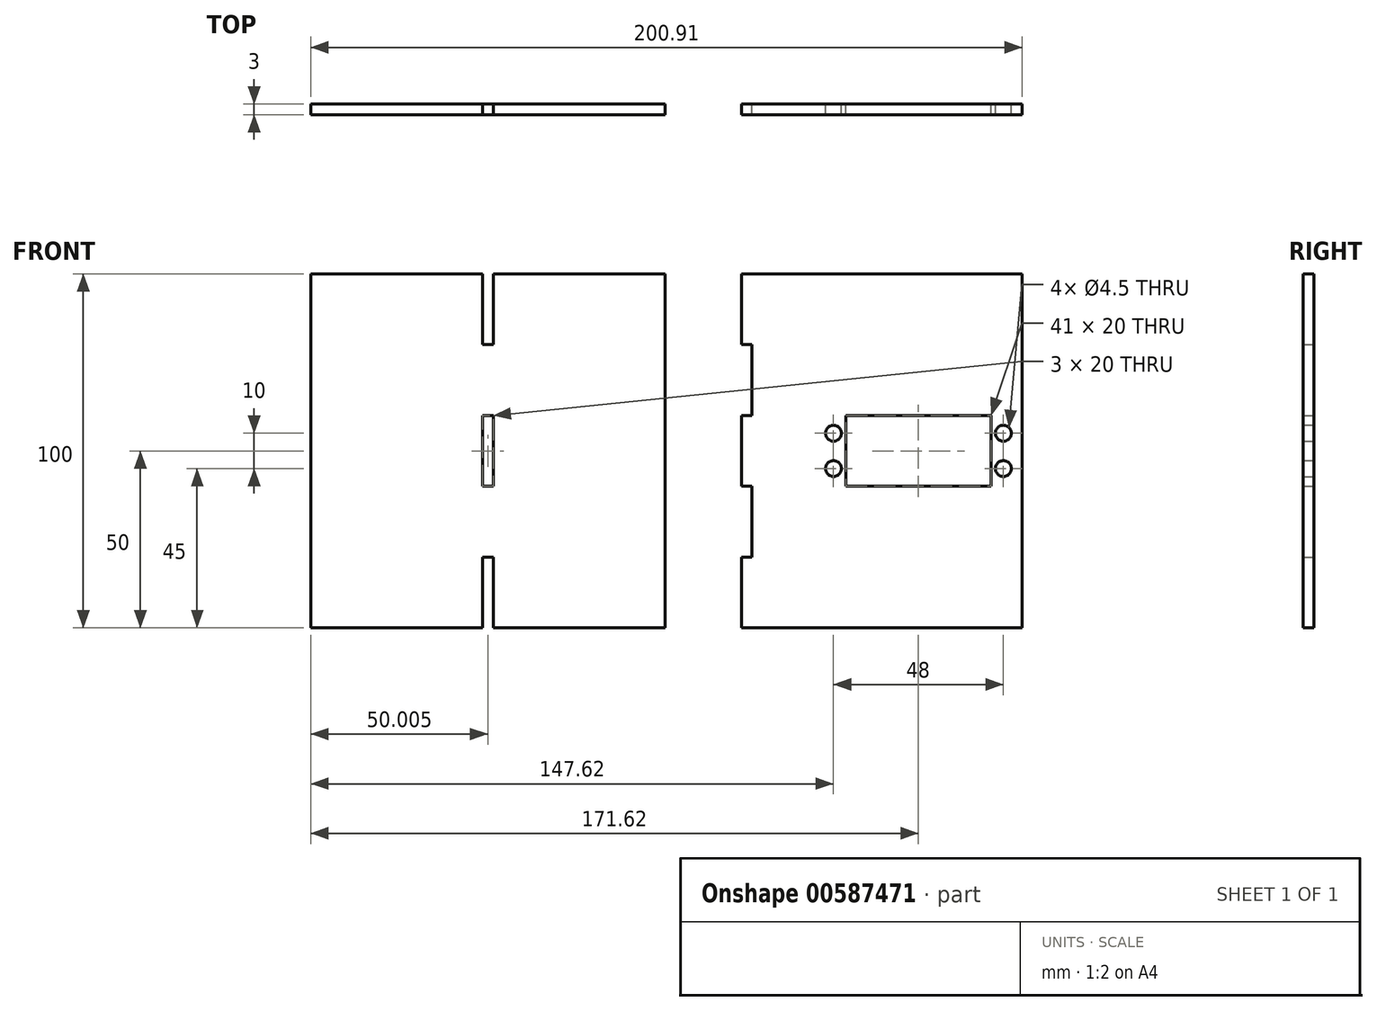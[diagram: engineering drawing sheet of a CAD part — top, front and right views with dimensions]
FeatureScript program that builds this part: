
annotation { "Feature Type Name" : "Feature", "Feature Type Description" : "" }
export const myFeature = defineFeature(function(context is Context, id is Id, definition is map)
    precondition{}
    {
        {
            var Q0;
            Q0=qCreatedBy(makeId("Front.planeOp"),FACE);
            var sketch = newSketch(context, id + "F0", { "sketchPlane" : qUnion([Q0])});
            skLineSegment(sketch, "E0.bottom", {"start": v(-20.5, 10) * mm, "end": v(20.5, 10) * mm});
            skLineSegment(sketch, "E0.top", {"start": v(-20.5, -10) * mm, "end": v(20.5, -10) * mm});
            skLineSegment(sketch, "E0.left", {"start": v(-20.5, 10) * mm, "end": v(-20.5, -10) * mm});
            skLineSegment(sketch, "E0.right", {"start": v(20.5, 10) * mm, "end": v(20.5, -10) * mm});
            skPoint(sketch, "E0.middle", {"position": v(0, 0) * mm});
            skLineSegment(sketch, "E1.bottom", {"start": v(-50, 50) * mm, "end": v(29.3, 50) * mm});
            skLineSegment(sketch, "E1.top", {"start": v(-50, -50) * mm, "end": v(29.3, -50) * mm});
            skLineSegment(sketch, "E1.left", {"start": v(-50, 50) * mm, "end": v(-50, 30) * mm});
            skLineSegment(sketch, "E2", {"start": v(-50, 30) * mm, "end": v(-47, 30) * mm});
            skLineSegment(sketch, "E3", {"start": v(-47, 30) * mm, "end": v(-47, 10) * mm});
            skLineSegment(sketch, "E4", {"start": v(-47, 10) * mm, "end": v(-50, 10) * mm});
            skLineSegment(sketch, "E5.trimOffspring", {"start": v(-50, 10) * mm, "end": v(-50, -10) * mm});
            skLineSegment(sketch, "E6", {"start": v(-50, -10) * mm, "end": v(-47, -10) * mm});
            skLineSegment(sketch, "E7", {"start": v(-47, -10) * mm, "end": v(-47, -30) * mm});
            skLineSegment(sketch, "E8", {"start": v(-47, -30) * mm, "end": v(-50, -30) * mm});
            skLineSegment(sketch, "E9.trimOffspring", {"start": v(-50, -30) * mm, "end": v(-50, -50) * mm});
            skCircle(sketch, "E10", {"center": v(-24, 5) * mm, "radius": 2.25 * mm});
            skCircle(sketch, "E11", {"center": v(-24, -5) * mm, "radius": 2.25 * mm});
            skCircle(sketch, "E12", {"center": v(24, 5) * mm, "radius": 2.25 * mm});
            skCircle(sketch, "E13", {"center": v(24, -5) * mm, "radius": 2.25 * mm});
            skLineSegment(sketch, "E14", {"start": v(29.3, 50) * mm, "end": v(29.3, -50) * mm});
            skPoint(sketch, "E1.right.start.orphan", {"position": v(50, 50) * mm});
            skPoint(sketch, "E15.orphan", {"position": v(50, -50) * mm});
            skLineSegment(sketch, "E16.bottom", {"start": v(-71.62, 50) * mm, "end": v(-120.12, 50) * mm});
            skLineSegment(sketch, "E16.top", {"start": v(-71.62, -50) * mm, "end": v(-120.12, -50) * mm});
            skLineSegment(sketch, "E16.left", {"start": v(-71.62, 50) * mm, "end": v(-71.62, -50) * mm});
            skLineSegment(sketch, "E16.right", {"start": v(-171.62, 50) * mm, "end": v(-171.62, -50) * mm});
            skLineSegment(sketch, "E17.top", {"start": v(-123.12, 30) * mm, "end": v(-120.12, 30) * mm});
            skLineSegment(sketch, "E17.left", {"start": v(-123.12, 50) * mm, "end": v(-123.12, 30) * mm});
            skLineSegment(sketch, "E17.right", {"start": v(-120.12, 50) * mm, "end": v(-120.12, 30) * mm});
            skLineSegment(sketch, "E18.bottom", {"start": v(-120.12, 10) * mm, "end": v(-123.12, 10) * mm});
            skLineSegment(sketch, "E18.top", {"start": v(-120.12, -10) * mm, "end": v(-123.12, -10) * mm});
            skLineSegment(sketch, "E18.left", {"start": v(-120.12, 10) * mm, "end": v(-120.12, -10) * mm});
            skLineSegment(sketch, "E18.right", {"start": v(-123.12, 10) * mm, "end": v(-123.12, -10) * mm});
            skLineSegment(sketch, "E19.bottom", {"start": v(-120.12, -30) * mm, "end": v(-123.12, -30) * mm});
            skLineSegment(sketch, "E19.left", {"start": v(-120.12, -30) * mm, "end": v(-120.12, -50) * mm});
            skLineSegment(sketch, "E19.right", {"start": v(-123.12, -30) * mm, "end": v(-123.12, -50) * mm});
            skLineSegment(sketch, "E20.trimOffspring", {"start": v(-123.12, 50) * mm, "end": v(-171.62, 50) * mm});
            skLineSegment(sketch, "E21.trimOffspring", {"start": v(-123.12, -50) * mm, "end": v(-171.62, -50) * mm});
            skSolve(sketch);
        }
        {
            var Q0;
            Q0 = qSketchRegion(id + "F0", true);
            extrude(context, id + "F1", {"entities" : qUnion([Q0]), "depth" : 3 * mm, "offsetDistance" : 25 * mm});
        }
    });
